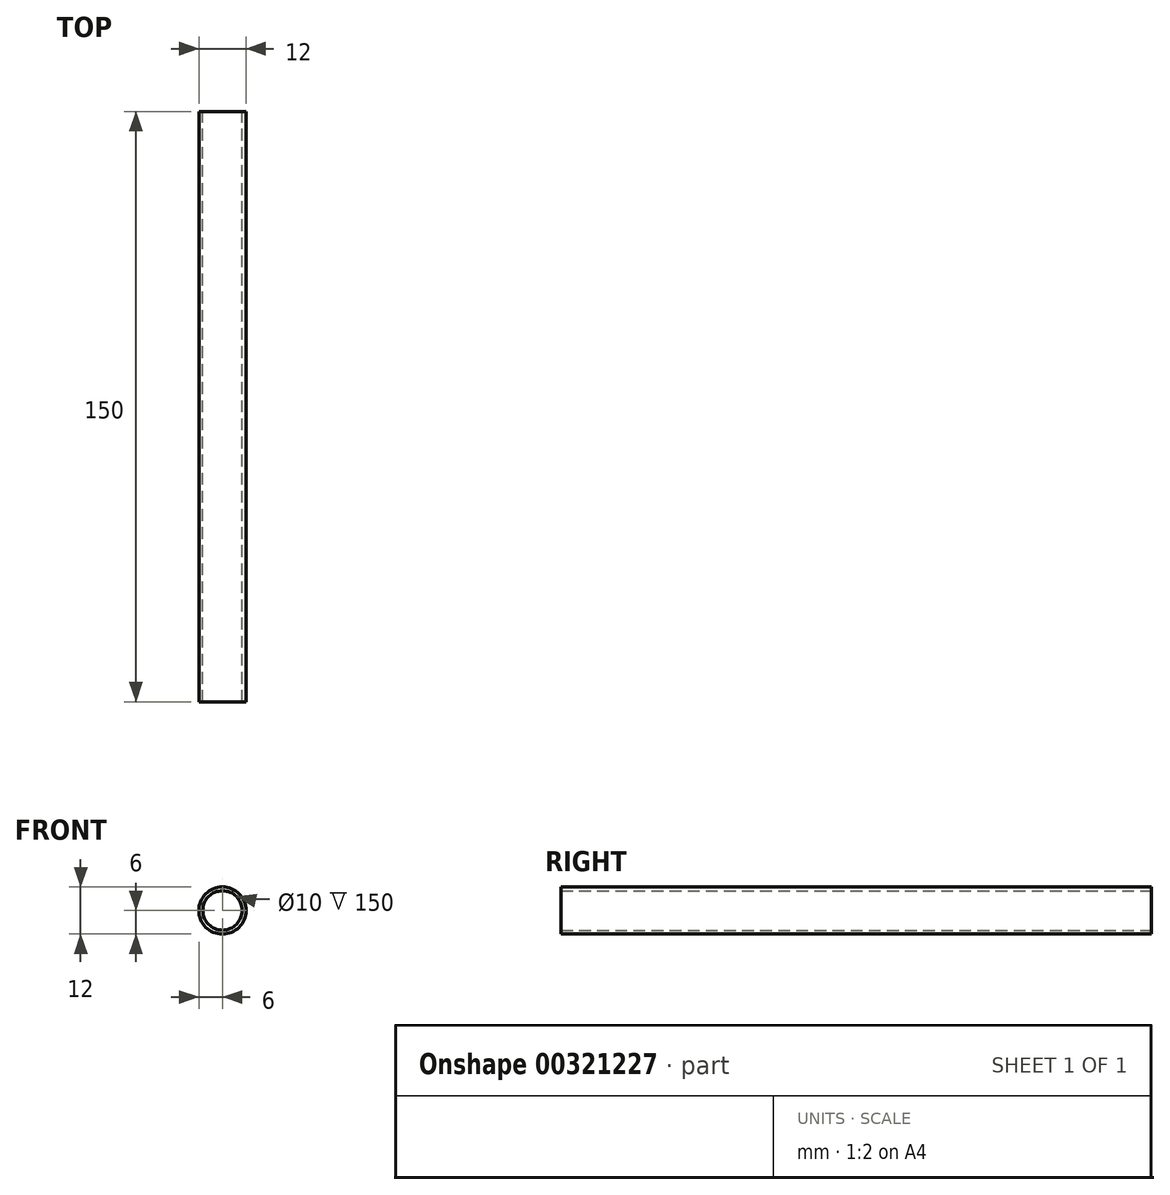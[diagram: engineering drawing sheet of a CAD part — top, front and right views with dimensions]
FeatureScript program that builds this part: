
annotation { "Feature Type Name" : "Feature", "Feature Type Description" : "" }
export const myFeature = defineFeature(function(context is Context, id is Id, definition is map)
    precondition{}
    {
        {
            var Q0;
            Q0=qCreatedBy(makeId("Front.planeOp"),FACE);
            var sketch = newSketch(context, id + "F0", { "sketchPlane" : qUnion([Q0])});
            skCircle(sketch, "E0", {"center": v(0, 0) * mm, "radius": 6 * mm});
            skCircle(sketch, "E1", {"center": v(0, 0) * mm, "radius": 5 * mm});
            skSolve(sketch);
        }
        {
            var Q0;
            Q0 = qSketchRegion(id + "F0", true);
            extrude(context, id + "F1", {"entities" : qUnion([Q0]), "depth" : 150 * mm});
        }
    });
